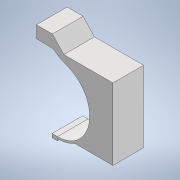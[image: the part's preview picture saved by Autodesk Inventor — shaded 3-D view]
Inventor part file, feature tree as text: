
AUTODESK INVENTOR PART (.ipt)
format: ipt  version: 2022 (Build 260153000, 153)  size: 127,488 bytes
history: native  units: in
note: dims shown in document units (in); Inventor stores cm internally (conversion verified against a paired STEP export)
features: other x4, reference x3, sheet_metal_op x1, sketch x1
ambient origin geometry x8: Origin, YZ Plane, XZ Plane, XY Plane, X Axis, Y Axis, Z Axis, Center Point
bodies: Body1 (feature_tree)
feature tree (9):
  sheet_metal_op  "Face2"
  sketch  "Sketch1"  dims[d1=0.12in]
  reference  "Reference11"
  reference  "Reference12"
  reference  "Reference13"
  other  "Plate2"
  parser-record x1  (decoder bookkeeping rows leaked as tree rows — omitted from the tree; the rows remain in map.json)
  other  "Assembly1.iam"
  other  "sheetmettaal:1"
note: 1 file-system path scrubbed to <path> (originals preserved in map.json)
